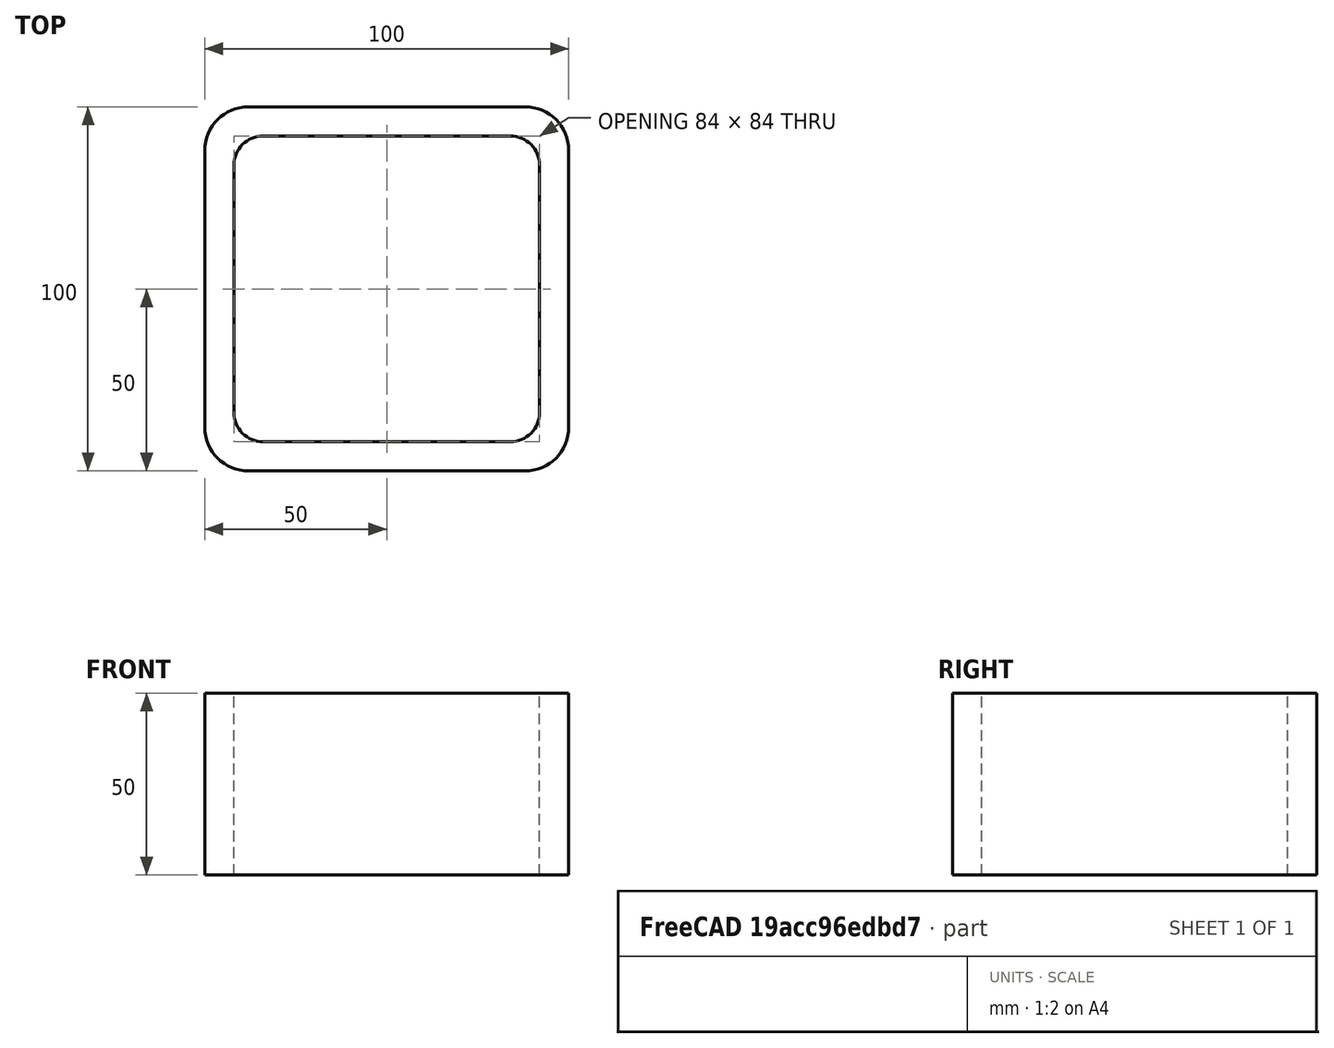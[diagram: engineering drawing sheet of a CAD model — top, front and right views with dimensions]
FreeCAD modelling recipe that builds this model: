
FCSTD DOCUMENT  (FreeCAD 0.15R4671 (Git))
Label: Square hollow section 100x100x8 EN10219 S235JRH
License: All rights reserved
LicenseURL: http://en.wikipedia.org/wiki/All_rights_reserved
objects: Sketcher::SketchObject×1, Part::Extrusion×1
note: 2 computed .brp shape members not serialized (recipe doc carries the construction recipe); baked Part::Feature solids carry a one-line shape summary decoded from their .brp

FEATURE [Sketcher::SketchObject] Sketch
  sketch-geometry (16):
    g0: LineSegment StartX=-34 StartY=42 StartZ=0 EndX=34 EndY=42 EndZ=0
    g1: LineSegment StartX=42 StartY=34 StartZ=0 EndX=42 EndY=-34 EndZ=0
    g2: LineSegment StartX=34 StartY=-42 StartZ=0 EndX=-34 EndY=-42 EndZ=0
    g3: LineSegment StartX=-42 StartY=-34 StartZ=0 EndX=-42 EndY=34 EndZ=0
    g4: LineSegment StartX=-38 StartY=50 StartZ=0 EndX=38 EndY=50 EndZ=0
    g5: LineSegment StartX=50 StartY=38 StartZ=0 EndX=50 EndY=-38 EndZ=0
    g6: LineSegment StartX=38 StartY=-50 StartZ=0 EndX=-38 EndY=-50 EndZ=0
    g7: LineSegment StartX=-50 StartY=-38 StartZ=0 EndX=-50 EndY=38 EndZ=0
    g8: ArcOfCircle CenterX=-34 CenterY=34 CenterZ=0 NormalX=0 NormalY=0 NormalZ=1 Radius=8 StartAngle=1.5708 EndAngle=3.14159
    g9: ArcOfCircle CenterX=34 CenterY=34 CenterZ=0 NormalX=0 NormalY=0 NormalZ=1 Radius=8 StartAngle=0 EndAngle=1.5708
    g10: ArcOfCircle CenterX=34 CenterY=-34 CenterZ=0 NormalX=0 NormalY=0 NormalZ=1 Radius=8 StartAngle=4.71239 EndAngle=6.28319
    g11: ArcOfCircle CenterX=-34 CenterY=-34 CenterZ=0 NormalX=0 NormalY=0 NormalZ=1 Radius=8 StartAngle=3.14159 EndAngle=4.71239
    g12: ArcOfCircle CenterX=38 CenterY=38 CenterZ=0 NormalX=0 NormalY=0 NormalZ=1 Radius=12 StartAngle=0 EndAngle=1.5708
    g13: ArcOfCircle CenterX=38 CenterY=-38 CenterZ=0 NormalX=0 NormalY=0 NormalZ=1 Radius=12 StartAngle=4.71239 EndAngle=6.28319
    g14: ArcOfCircle CenterX=-38 CenterY=-38 CenterZ=0 NormalX=0 NormalY=0 NormalZ=1 Radius=12 StartAngle=3.14159 EndAngle=4.71239
    g15: ArcOfCircle CenterX=-38 CenterY=38 CenterZ=0 NormalX=0 NormalY=0 NormalZ=1 Radius=12 StartAngle=1.5708 EndAngle=3.14159
  constraints (36):
    c: Horizontal(g2)
    c: Vertical(g3)
    c: Horizontal(g6)
    c: Vertical(g7)
    c: Tangent(g3,g8) = 1.5708
    c: Tangent(g0,g8) = 1.5708
    c: Tangent(g0,g9) = 1.5708
    c: Tangent(g1,g9) = 1.5708
    c: Tangent(g1,g10) = 1.5708
    c: Tangent(g2,g10) = 1.5708
    c: Tangent(g2,g11) = 1.5708
    c: Tangent(g3,g11) = 1.5708
    c: Tangent(g4,g12) = 1.5708
    c: Tangent(g5,g12) = 1.5708
    c: Tangent(g5,g13) = 1.5708
    c: Tangent(g6,g13) = 1.5708
    c: Tangent(g6,g14) = 1.5708
    c: Tangent(g7,g14) = 1.5708
    c: Tangent(g7,g15) = 1.5708
    c: Tangent(g4,g15) = 1.5708
    c: Equal(g9,g8)
    c: Equal(g9,g11)
    c: Equal(g9,g10)
    c: Equal(g12,g15)
    c: Equal(g12,g14)
    c: Equal(g12,g13)
    c: Symmetric(g4,g6,g-1)
    c: Symmetric(g7,g5,g-2)
    c: DistanceY(g4,g6) = -100
    c: DistanceX(g7,g5) = 100
    c: Symmetric(g3,g1,g-2)
    c: Symmetric(g0,g2,g-1)
    c: DistanceY(g0,g4) = 8
    c: DistanceX(g5,g1) = -8
    c: Radius(g9) = 8
    c: Radius(g12) = 12
FEATURE [Part::Extrusion] Extrude  label="Square hollow section 100x100x8 EN10219 S235JRH"
  Base = -> Sketch
  Dir = (0,0,50)
  Solid = true
